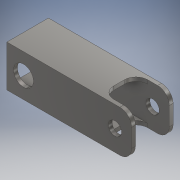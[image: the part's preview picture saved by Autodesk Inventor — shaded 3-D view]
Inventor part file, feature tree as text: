
AUTODESK INVENTOR PART (.ipt)
format: ipt  version: 2018.2 (Build 222227000, 227)  size: 166,400 bytes
history: native  units: mm
features: extrude x5, sketch x5, other x1, fillet x1
ambient origin geometry x8: Origin, YZ Plane, XZ Plane, XY Plane, X Axis, Y Axis, Z Axis, Center Point
bodies: Body1 (feature_tree)
feature tree (12):
  other  "ソリッド1"
  extrude  "押し出し1"  Depth=25.0mm
  extrude  "押し出し2"  Depth=25.0mm
  extrude  "押し出し3"  Depth=75.0mm TaperAngle=0.0deg
  extrude  "押し出し4"  Depth=12.0mm
  extrude  "押し出し5"  Depth=10.0mm
  fillet  "フィレット1"  Radius=12.5mm
  sketch  "スケッチ1"
  sketch  "スケッチ2"
  sketch  "スケッチ3"
  sketch  "スケッチ4"
  sketch  "スケッチ5"
